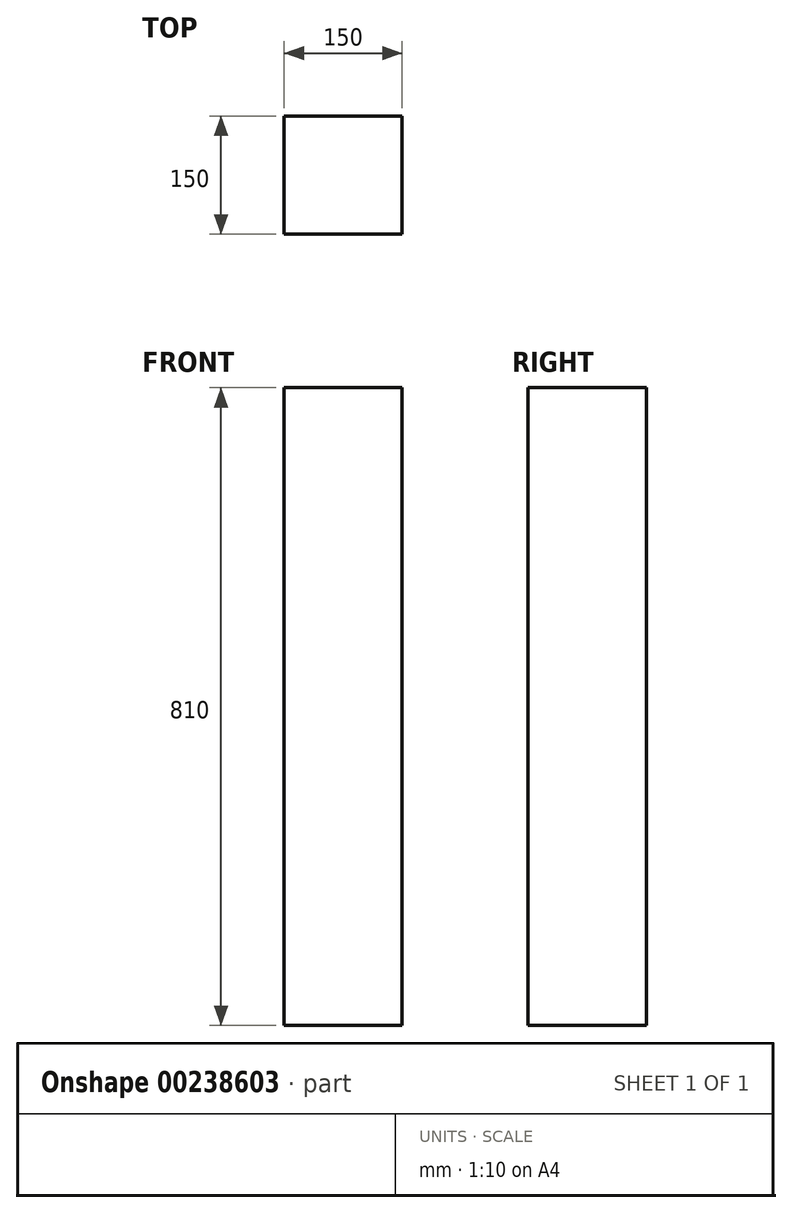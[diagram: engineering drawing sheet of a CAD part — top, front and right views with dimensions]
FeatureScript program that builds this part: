
annotation { "Feature Type Name" : "Feature", "Feature Type Description" : "" }
export const myFeature = defineFeature(function(context is Context, id is Id, definition is map)
    precondition{}
    {
        {
            var Q0;
            Q0=qCreatedBy(makeId("Top.planeOp"),FACE);
            var sketch = newSketch(context, id + "F0", { "sketchPlane" : qUnion([Q0])});
            skLineSegment(sketch, "E0.bottom", {"start": v(75, -75) * mm, "end": v(-75, -75) * mm});
            skLineSegment(sketch, "E0.top", {"start": v(75, 75) * mm, "end": v(-75, 75) * mm});
            skLineSegment(sketch, "E0.left", {"start": v(75, -75) * mm, "end": v(75, 75) * mm});
            skLineSegment(sketch, "E0.right", {"start": v(-75, -75) * mm, "end": v(-75, 75) * mm});
            skPoint(sketch, "E0.middle", {"position": v(0, 0) * mm});
            skSolve(sketch);
        }
        {
            var Q0;
            Q0=makeQuery(id+"F0.imprint","IMPRINT",FACE,{"disambiguationData":[TD([[makeQuery(id+"F0.imprint","IMPRINT",EDGE,{"derivedFrom":sQuery(id+"F0.wireOp",EDGE,"E0.bottom")}),-1.0]])]});
            extrude(context, id + "F1", {"entities" : qUnion([Q0]), "depth" : 810 * mm});
        }
    });
